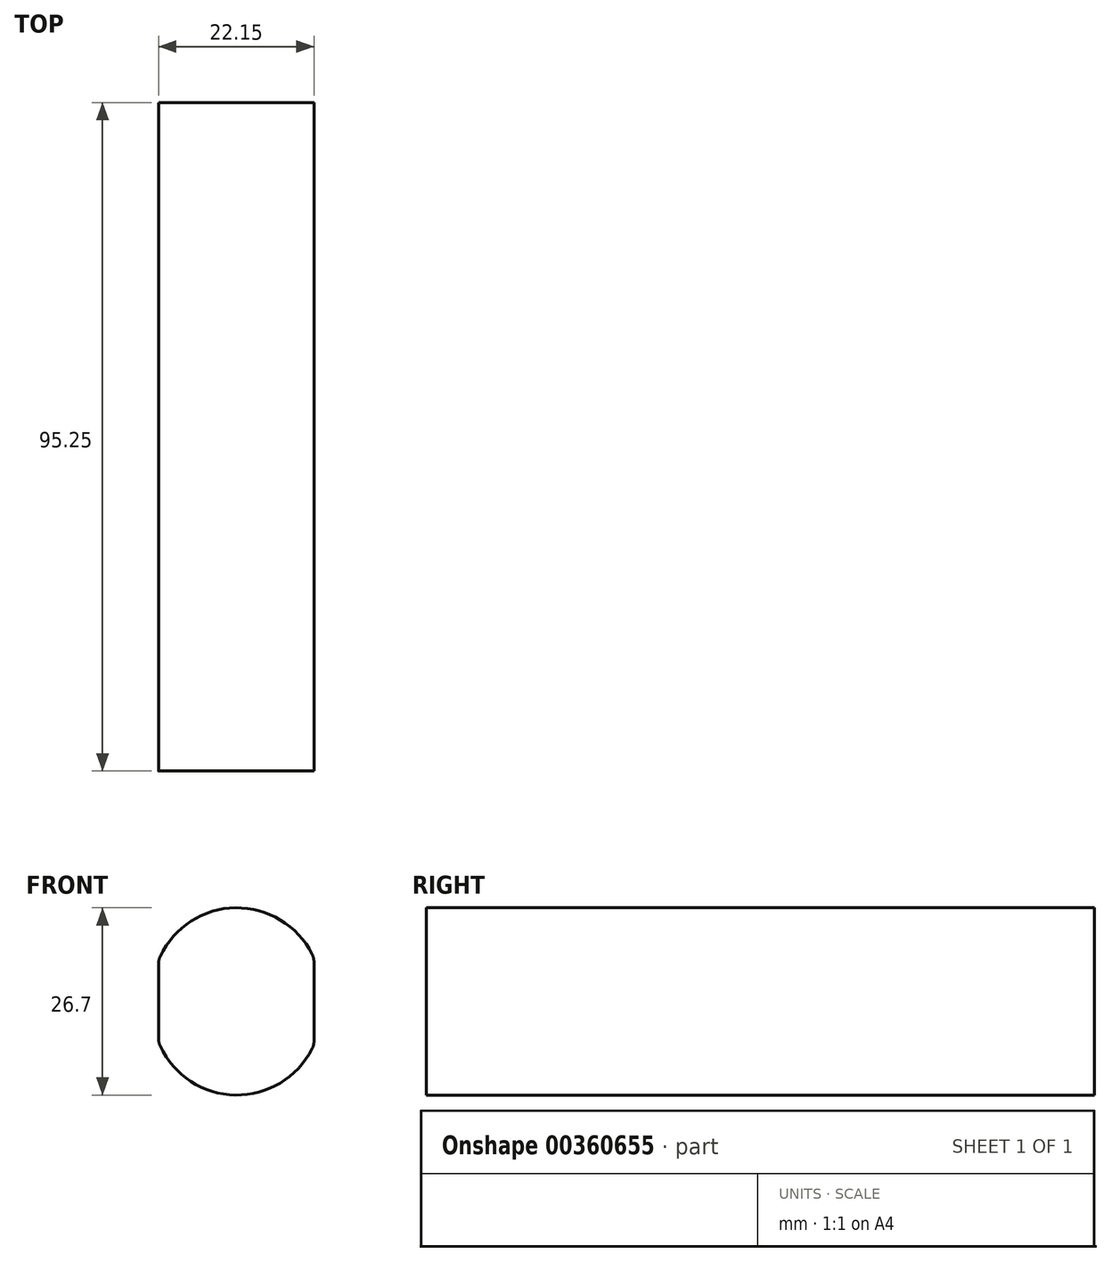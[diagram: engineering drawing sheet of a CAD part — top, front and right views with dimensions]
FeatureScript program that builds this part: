
annotation { "Feature Type Name" : "Feature", "Feature Type Description" : "" }
export const myFeature = defineFeature(function(context is Context, id is Id, definition is map)
    precondition{}
    {
        {
            var Q0;
            Q0=qCreatedBy(makeId("Front.planeOp"),FACE);
            var sketch = newSketch(context, id + "F0", { "sketchPlane" : qUnion([Q0])});
            skLineSegment(sketch, "E0.left", {"start": v(-14.1, 1.1) * mm, "end": v(-14.1, -9.6) * mm});
            skLineSegment(sketch, "E0.right", {"start": v(8.05, 1.32) * mm, "end": v(8.05, -9.9) * mm});
            skArc(sketch, "E1", {"start": v(7.78, 2.47) * mm, "mid": v(-3.13, 9.07) * mm, "end": v(-13.86, 2.18) * mm});
            skArc(sketch, "E2", {"start": v(-13.86, -10.67) * mm, "mid": v(-3.17, -17.62) * mm, "end": v(7.77, -11.06) * mm});
            skPoint(sketch, "E3.newPointB", {"position": v(-14.04, 1.76) * mm});
            skArc(sketch, "E3.filletArc", {"start": v(-13.86, 2.18) * mm, "mid": v(-14.04, 1.65) * mm, "end": v(-14.1, 1.1) * mm});
            skPoint(sketch, "E4.newPointB", {"position": v(8.1, 1.76) * mm});
            skArc(sketch, "E4.filletArc", {"start": v(8.05, 1.32) * mm, "mid": v(7.98, 1.9) * mm, "end": v(7.78, 2.47) * mm});
            skPoint(sketch, "E5.newPointA", {"position": v(8.12, -10.3) * mm});
            skArc(sketch, "E5.filletArc", {"start": v(7.77, -11.06) * mm, "mid": v(7.98, -10.5) * mm, "end": v(8.05, -9.9) * mm});
            skPoint(sketch, "E6.newPointA", {"position": v(-14.02, -10.3) * mm});
            skArc(sketch, "E6.filletArc", {"start": v(-14.1, -9.6) * mm, "mid": v(-14.04, -10.15) * mm, "end": v(-13.86, -10.67) * mm});
            skSolve(sketch);
        }
        {
            var Q0;
            Q0 = qSketchRegion(id + "F0", true);
            extrude(context, id + "F1", {"entities" : qUnion([Q0]), "depth" : 95.25 * mm});
        }
    });
